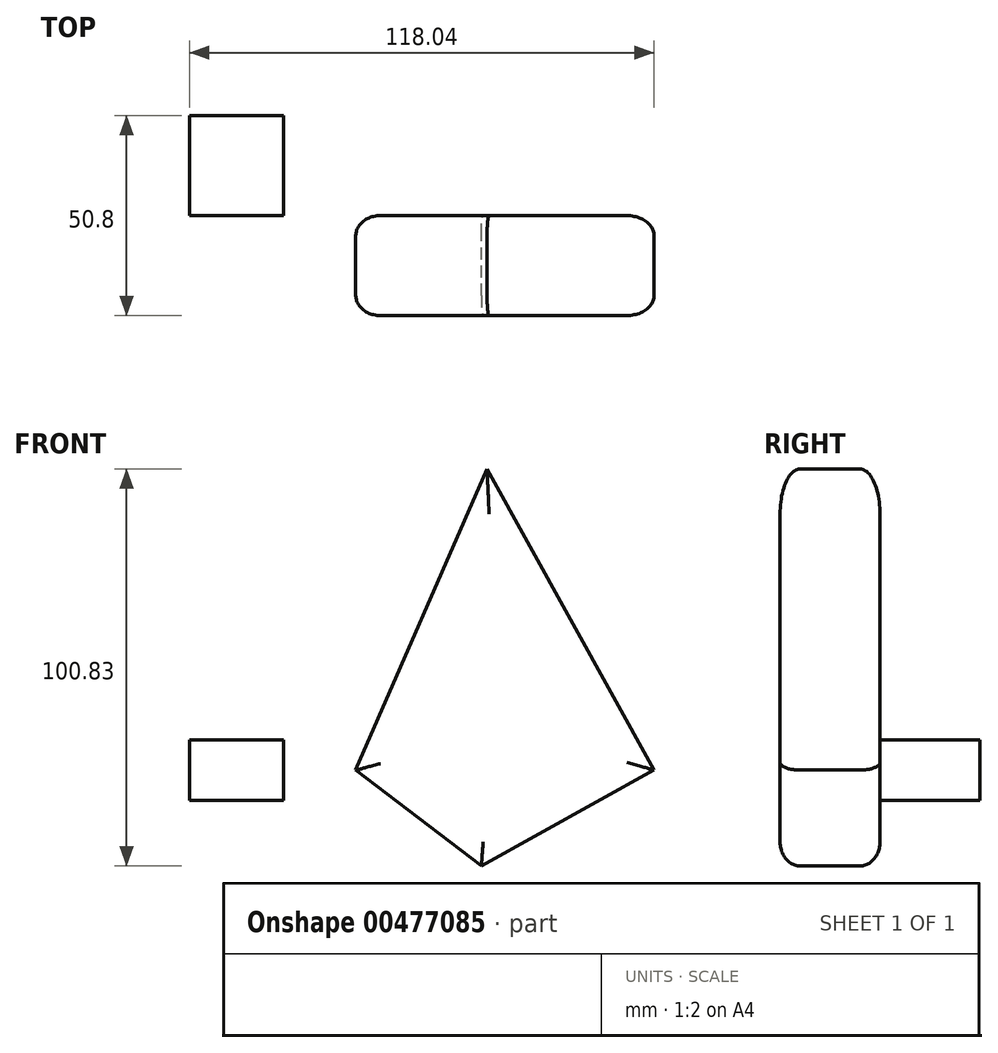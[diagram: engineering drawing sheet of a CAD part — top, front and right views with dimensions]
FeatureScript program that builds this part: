
annotation { "Feature Type Name" : "Feature", "Feature Type Description" : "" }
export const myFeature = defineFeature(function(context is Context, id is Id, definition is map)
    precondition{}
    {
        {
            var Q0;
            Q0=qCreatedBy(makeId("Front.planeOp"),FACE);
            var sketch = newSketch(context, id + "F0", { "sketchPlane" : qUnion([Q0])});
            skLineSegment(sketch, "E0", {"start": v(0, 0) * mm, "end": v(33.35, 76.5) * mm});
            skLineSegment(sketch, "E1", {"start": v(33.35, 76.5) * mm, "end": v(75.79, 0) * mm});
            skLineSegment(sketch, "E2", {"start": v(75.79, 0) * mm, "end": v(31.92, -24.34) * mm});
            skLineSegment(sketch, "E3", {"start": v(31.92, -24.34) * mm, "end": v(0, 0) * mm});
            skSolve(sketch);
        }
        {
            var Q0;
            Q0 = qSketchRegion(id + "F0", true);
            extrude(context, id + "F1", {"entities" : qUnion([Q0]), "depth" : 25.4 * mm});
        }
        {
            var Q0;
            Q0=makeQuery(id+"F1.opExtrude","CAP_FACE",FACE,{"disambiguationData":[OSD([sQuery(id+"F0.wireOp",EDGE,"E0"),sQuery(id+"F0.wireOp",EDGE,"E1"),sQuery(id+"F0.wireOp",EDGE,"E2"),sQuery(id+"F0.wireOp",EDGE,"E3")])],"isStart":false});
            var Q1;
            Q1=makeQuery(id+"F1.opExtrude","CAP_FACE",FACE,{"disambiguationData":[OSD([sQuery(id+"F0.wireOp",EDGE,"E0"),sQuery(id+"F0.wireOp",EDGE,"E1"),sQuery(id+"F0.wireOp",EDGE,"E2"),sQuery(id+"F0.wireOp",EDGE,"E3")])],"isStart":true});
            fillet(context, id + "F2", {"entities" : qUnion([Q0, Q1]), "radius" : 5.08 * mm, "tangentPropagation" : true, "allowEdgeOverflow" : false});
        }
        {
            var Q0;
            Q0=qCreatedBy(makeId("Front.planeOp"),FACE);
            var sketch = newSketch(context, id + "F3", { "sketchPlane" : qUnion([Q0])});
            skLineSegment(sketch, "E4.bottom", {"start": v(-42.25, 7.64) * mm, "end": v(-18.4, 7.64) * mm});
            skLineSegment(sketch, "E4.top", {"start": v(-42.25, -7.64) * mm, "end": v(-18.4, -7.64) * mm});
            skLineSegment(sketch, "E4.left", {"start": v(-42.25, 7.64) * mm, "end": v(-42.25, -7.64) * mm});
            skLineSegment(sketch, "E4.right", {"start": v(-18.4, 7.64) * mm, "end": v(-18.4, -7.64) * mm});
            skPoint(sketch, "E4.middle", {"position": v(-30.33, 0) * mm});
            skPoint(sketch, "E5.middle", {"position": v(-42.83, -14.4) * mm});
            skSolve(sketch);
        }
        {
            var Q0;
            Q0=makeQuery(id+"F3.imprint","IMPRINT",FACE,{"disambiguationData":[TD([[makeQuery(id+"F3.imprint","IMPRINT",EDGE,{"derivedFrom":sQuery(id+"F3.wireOp",EDGE,"E4.bottom")}),-1.0]])]});
            extrude(context, id + "F4", {"entities" : qUnion([Q0]), "oppositeDirection" : true, "depth" : 25.4 * mm});
        }
    });
